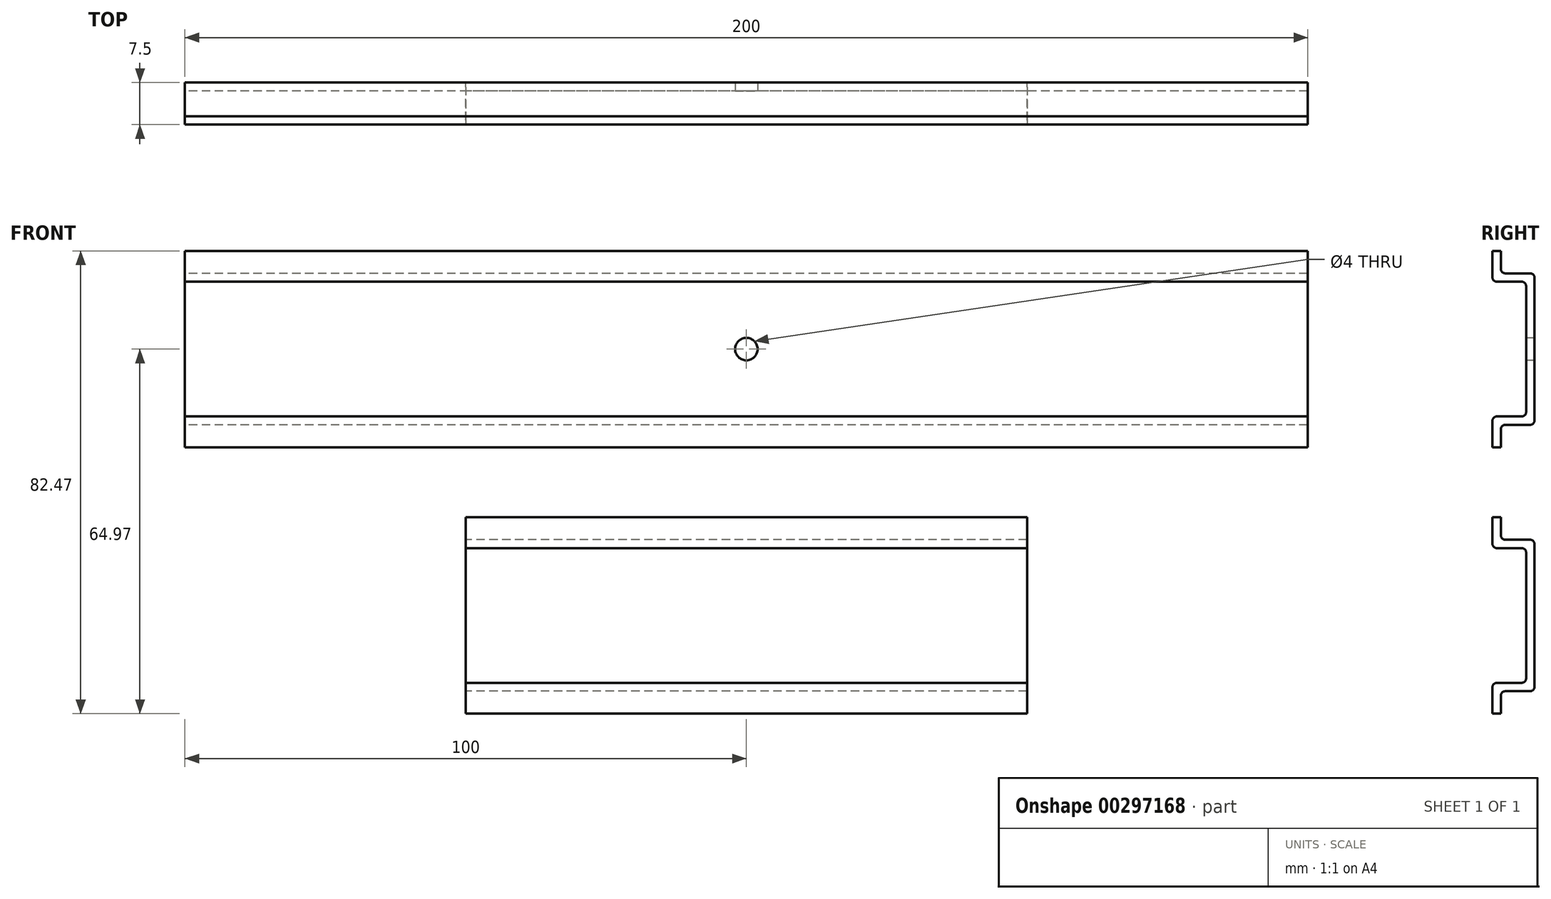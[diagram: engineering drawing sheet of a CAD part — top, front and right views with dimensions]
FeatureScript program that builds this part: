
annotation { "Feature Type Name" : "Feature", "Feature Type Description" : "" }
export const myFeature = defineFeature(function(context is Context, id is Id, definition is map)
    precondition{}
    {
        {
            var Q0;
            Q0=qCreatedBy(makeId("Right.planeOp"),FACE);
            var sketch = newSketch(context, id + "F0", { "sketchPlane" : qUnion([Q0])});
            skLineSegment(sketch, "E0", {"start": v(0, 0) * mm, "end": v(0, 12.7) * mm});
            skLineSegment(sketch, "E1", {"start": v(-0.8, 13.5) * mm, "end": v(-5.2, 13.5) * mm});
            skLineSegment(sketch, "E2", {"start": v(-6, 17.5) * mm, "end": v(-7.5, 17.5) * mm});
            skLineSegment(sketch, "E3", {"start": v(-7.5, 17.5) * mm, "end": v(-7.5, 12.8) * mm});
            skLineSegment(sketch, "E4", {"start": v(-6.7, 12) * mm, "end": v(-2.3, 12) * mm});
            skLineSegment(sketch, "E5", {"start": v(-1.5, 11.2) * mm, "end": v(-1.5, 0) * mm});
            skLineSegment(sketch, "E6", {"start": v(-6, 17.5) * mm, "end": v(-6, 14.3) * mm});
            skPoint(sketch, "E7.visualSharp", {"position": v(-7.5, 12) * mm});
            skArc(sketch, "E7.filletArc", {"start": v(-7.5, 12.8) * mm, "mid": v(-7.27, 12.23) * mm, "end": v(-6.7, 12) * mm});
            skPoint(sketch, "E8.visualSharp", {"position": v(-6, 13.5) * mm});
            skArc(sketch, "E8.filletArc", {"start": v(-6, 14.3) * mm, "mid": v(-5.77, 13.73) * mm, "end": v(-5.2, 13.5) * mm});
            skPoint(sketch, "E9.visualSharp", {"position": v(0, 13.5) * mm});
            skArc(sketch, "E9.filletArc", {"start": v(0, 12.7) * mm, "mid": v(-0.23, 13.27) * mm, "end": v(-0.8, 13.5) * mm});
            skPoint(sketch, "E10.visualSharp", {"position": v(-1.5, 12) * mm});
            skArc(sketch, "E10.filletArc", {"start": v(-1.5, 11.2) * mm, "mid": v(-1.73, 11.77) * mm, "end": v(-2.3, 12) * mm});
            skLineSegment(sketch, "E11.MirrorCS", {"start": v(0, 0) * mm, "end": v(0, -12.7) * mm});
            skPoint(sketch, "E12.MirrorP", {"position": v(0, -13.5) * mm});
            skLineSegment(sketch, "E13.MirrorCS", {"start": v(-0.8, -13.5) * mm, "end": v(-5.2, -13.5) * mm});
            skArc(sketch, "E14.MirrorCS", {"start": v(-6, -14.3) * mm, "mid": v(-5.77, -13.73) * mm, "end": v(-5.2, -13.5) * mm});
            skLineSegment(sketch, "E15.MirrorCS", {"start": v(-6, -17.5) * mm, "end": v(-6, -14.3) * mm});
            skLineSegment(sketch, "E16.MirrorCS", {"start": v(-6, -17.5) * mm, "end": v(-7.5, -17.5) * mm});
            skLineSegment(sketch, "E17.MirrorCS", {"start": v(-7.5, -17.5) * mm, "end": v(-7.5, -12.8) * mm});
            skArc(sketch, "E18.MirrorCS", {"start": v(-7.5, -12.8) * mm, "mid": v(-7.27, -12.23) * mm, "end": v(-6.7, -12) * mm});
            skLineSegment(sketch, "E19.MirrorCS", {"start": v(-6.7, -12) * mm, "end": v(-2.3, -12) * mm});
            skArc(sketch, "E20.MirrorCS", {"start": v(-1.5, -11.2) * mm, "mid": v(-1.73, -11.77) * mm, "end": v(-2.3, -12) * mm});
            skLineSegment(sketch, "E21.MirrorCS", {"start": v(-1.5, -11.2) * mm, "end": v(-1.5, 0) * mm});
            skArc(sketch, "E22.MirrorCS", {"start": v(0, -12.7) * mm, "mid": v(-0.23, -13.27) * mm, "end": v(-0.8, -13.5) * mm});
            skSolve(sketch);
        }
        {
            var Q0;
            Q0=makeQuery(id+"F0.imprint","IMPRINT",FACE,{"disambiguationData":[TD([[makeQuery(id+"F0.imprint","IMPRINT",EDGE,{"derivedFrom":sQuery(id+"F0.wireOp",EDGE,"E0")}),1.0]])]});
            extrude(context, id + "F1", {"entities" : qUnion([Q0]), "depth" : 200 * mm, "symmetric" : true});
        }
        {
            var Q0;
            Q0=makeQuery(id+"F1.opExtrude","SWEPT_FACE",FACE,{"disambiguationData":[OSD([sQuery(id+"F0.wireOp",EDGE,"E5"),sQuery(id+"F0.wireOp",EDGE,"E21.MirrorCS")])]});
            var sketch = newSketch(context, id + "F2", { "sketchPlane" : qUnion([Q0])});
            skCircle(sketch, "E23", {"center": v(0, 0) * mm, "radius": 2 * mm});
            skSolve(sketch);
        }
        {
            var Q0;
            Q0=makeQuery(id+"F2.imprint","IMPRINT",FACE,{"disambiguationData":[TD([[makeQuery(id+"F2.imprint","IMPRINT",EDGE,{"derivedFrom":sQuery(id+"F2.wireOp",EDGE,"E23")}),1.0]])]});
            extrude(context, id + "F3", {"entities" : qUnion([Q0]), "operationType" : NewBodyOperationType.REMOVE, "endBound" : BoundingType.THROUGH_ALL, "oppositeDirection" : true, "depth" : 25 * mm});
        }
        {
            var Q0;
            Q0=makeQuery(id+"F1.opExtrude","SWEPT_BODY",BODY,{"disambiguationData":[OSD([sQuery(id+"F0.wireOp",EDGE,"E0"),sQuery(id+"F0.wireOp",EDGE,"E1"),sQuery(id+"F0.wireOp",EDGE,"E2"),sQuery(id+"F0.wireOp",EDGE,"E3"),sQuery(id+"F0.wireOp",EDGE,"E4"),sQuery(id+"F0.wireOp",EDGE,"E5"),sQuery(id+"F0.wireOp",EDGE,"E6"),sQuery(id+"F0.wireOp",EDGE,"E7.filletArc"),sQuery(id+"F0.wireOp",EDGE,"E8.filletArc"),sQuery(id+"F0.wireOp",EDGE,"E9.filletArc"),sQuery(id+"F0.wireOp",EDGE,"E10.filletArc"),sQuery(id+"F0.wireOp",EDGE,"E11.MirrorCS"),sQuery(id+"F0.wireOp",EDGE,"E13.MirrorCS"),sQuery(id+"F0.wireOp",EDGE,"E14.MirrorCS"),sQuery(id+"F0.wireOp",EDGE,"E15.MirrorCS"),sQuery(id+"F0.wireOp",EDGE,"E16.MirrorCS"),sQuery(id+"F0.wireOp",EDGE,"E17.MirrorCS"),sQuery(id+"F0.wireOp",EDGE,"E18.MirrorCS"),sQuery(id+"F0.wireOp",EDGE,"E19.MirrorCS"),sQuery(id+"F0.wireOp",EDGE,"E20.MirrorCS"),sQuery(id+"F0.wireOp",EDGE,"E21.MirrorCS"),sQuery(id+"F0.wireOp",EDGE,"E22.MirrorCS")])]});
            transform(context, id + "F4", {"entities" : qUnion([Q0]), "transformType" : TransformType.TRANSLATION_3D, "dx" : 0 * mm, "dy" : 0 * mm, "dz" : -65 * mm, "makeCopy" : true});
        }
        {
            var Q0;
            Q0=makeQuery(id+"F4.opPattern","COPY",BODY,{"derivedFrom":makeQuery(id+"F1.opExtrude","SWEPT_BODY",BODY,{"disambiguationData":[OSD([sQuery(id+"F0.wireOp",EDGE,"E0"),sQuery(id+"F0.wireOp",EDGE,"E1"),sQuery(id+"F0.wireOp",EDGE,"E2"),sQuery(id+"F0.wireOp",EDGE,"E3"),sQuery(id+"F0.wireOp",EDGE,"E4"),sQuery(id+"F0.wireOp",EDGE,"E5"),sQuery(id+"F0.wireOp",EDGE,"E6"),sQuery(id+"F0.wireOp",EDGE,"E7.filletArc"),sQuery(id+"F0.wireOp",EDGE,"E8.filletArc"),sQuery(id+"F0.wireOp",EDGE,"E9.filletArc"),sQuery(id+"F0.wireOp",EDGE,"E10.filletArc"),sQuery(id+"F0.wireOp",EDGE,"E11.MirrorCS"),sQuery(id+"F0.wireOp",EDGE,"E13.MirrorCS"),sQuery(id+"F0.wireOp",EDGE,"E14.MirrorCS"),sQuery(id+"F0.wireOp",EDGE,"E15.MirrorCS"),sQuery(id+"F0.wireOp",EDGE,"E16.MirrorCS"),sQuery(id+"F0.wireOp",EDGE,"E17.MirrorCS"),sQuery(id+"F0.wireOp",EDGE,"E18.MirrorCS"),sQuery(id+"F0.wireOp",EDGE,"E19.MirrorCS"),sQuery(id+"F0.wireOp",EDGE,"E20.MirrorCS"),sQuery(id+"F0.wireOp",EDGE,"E21.MirrorCS"),sQuery(id+"F0.wireOp",EDGE,"E22.MirrorCS")])]}),"instanceName":"1"});
            deleteBodies(context, id + "F5", {"entities" : qUnion([Q0])});
        }
        {
            var Q0;
            Q0=qCreatedBy(makeId("Right.planeOp"),FACE);
            var sketch = newSketch(context, id + "F6", { "sketchPlane" : qUnion([Q0])});
            skLineSegment(sketch, "E24", {"start": v(0, -47.47) * mm, "end": v(0, -34.77) * mm});
            skLineSegment(sketch, "E25", {"start": v(-0.8, -33.97) * mm, "end": v(-5.2, -33.97) * mm});
            skLineSegment(sketch, "E26", {"start": v(-6, -29.97) * mm, "end": v(-7.5, -29.97) * mm});
            skLineSegment(sketch, "E27", {"start": v(-7.5, -29.97) * mm, "end": v(-7.5, -34.67) * mm});
            skLineSegment(sketch, "E28", {"start": v(-6.7, -35.47) * mm, "end": v(-2.3, -35.47) * mm});
            skLineSegment(sketch, "E29", {"start": v(-1.5, -36.27) * mm, "end": v(-1.5, -47.47) * mm});
            skLineSegment(sketch, "E30", {"start": v(-6, -29.97) * mm, "end": v(-6, -33.17) * mm});
            skPoint(sketch, "E31.visualSharp", {"position": v(-7.5, -35.47) * mm});
            skArc(sketch, "E31.filletArc", {"start": v(-7.5, -34.67) * mm, "mid": v(-7.27, -35.23) * mm, "end": v(-6.7, -35.47) * mm});
            skPoint(sketch, "E32.visualSharp", {"position": v(-6, -33.97) * mm});
            skArc(sketch, "E32.filletArc", {"start": v(-6, -33.17) * mm, "mid": v(-5.77, -33.73) * mm, "end": v(-5.2, -33.97) * mm});
            skPoint(sketch, "E33.visualSharp", {"position": v(0, -33.97) * mm});
            skArc(sketch, "E33.filletArc", {"start": v(0, -34.77) * mm, "mid": v(-0.23, -34.2) * mm, "end": v(-0.8, -33.97) * mm});
            skPoint(sketch, "E34.visualSharp", {"position": v(-1.5, -35.47) * mm});
            skArc(sketch, "E34.filletArc", {"start": v(-1.5, -36.27) * mm, "mid": v(-1.73, -35.7) * mm, "end": v(-2.3, -35.47) * mm});
            skLineSegment(sketch, "E35.MirrorCS", {"start": v(0, -47.47) * mm, "end": v(0, -60.17) * mm});
            skPoint(sketch, "E36.MirrorP", {"position": v(0, -60.97) * mm});
            skLineSegment(sketch, "E37.MirrorCS", {"start": v(-0.8, -60.97) * mm, "end": v(-5.2, -60.97) * mm});
            skArc(sketch, "E38.MirrorCS", {"start": v(-6, -61.77) * mm, "mid": v(-5.77, -61.2) * mm, "end": v(-5.2, -60.97) * mm});
            skLineSegment(sketch, "E39.MirrorCS", {"start": v(-6, -64.97) * mm, "end": v(-6, -61.77) * mm});
            skLineSegment(sketch, "E40.MirrorCS", {"start": v(-6, -64.97) * mm, "end": v(-7.5, -64.97) * mm});
            skLineSegment(sketch, "E41.MirrorCS", {"start": v(-7.5, -64.97) * mm, "end": v(-7.5, -60.27) * mm});
            skArc(sketch, "E42.MirrorCS", {"start": v(-7.5, -60.27) * mm, "mid": v(-7.27, -59.7) * mm, "end": v(-6.7, -59.47) * mm});
            skLineSegment(sketch, "E43.MirrorCS", {"start": v(-6.7, -59.47) * mm, "end": v(-2.3, -59.47) * mm});
            skArc(sketch, "E44.MirrorCS", {"start": v(-1.5, -58.67) * mm, "mid": v(-1.73, -59.23) * mm, "end": v(-2.3, -59.47) * mm});
            skLineSegment(sketch, "E45.MirrorCS", {"start": v(-1.5, -58.67) * mm, "end": v(-1.5, -47.47) * mm});
            skArc(sketch, "E46.MirrorCS", {"start": v(0, -60.17) * mm, "mid": v(-0.23, -60.73) * mm, "end": v(-0.8, -60.97) * mm});
            skSolve(sketch);
        }
        {
            var Q0;
            Q0=makeQuery(id+"F6.imprint","IMPRINT",FACE,{"disambiguationData":[TD([[makeQuery(id+"F6.imprint","IMPRINT",EDGE,{"derivedFrom":sQuery(id+"F6.wireOp",EDGE,"E24")}),1.0]])]});
            extrude(context, id + "F7", {"entities" : qUnion([Q0]), "depth" : 100 * mm, "symmetric" : true});
        }
    });
